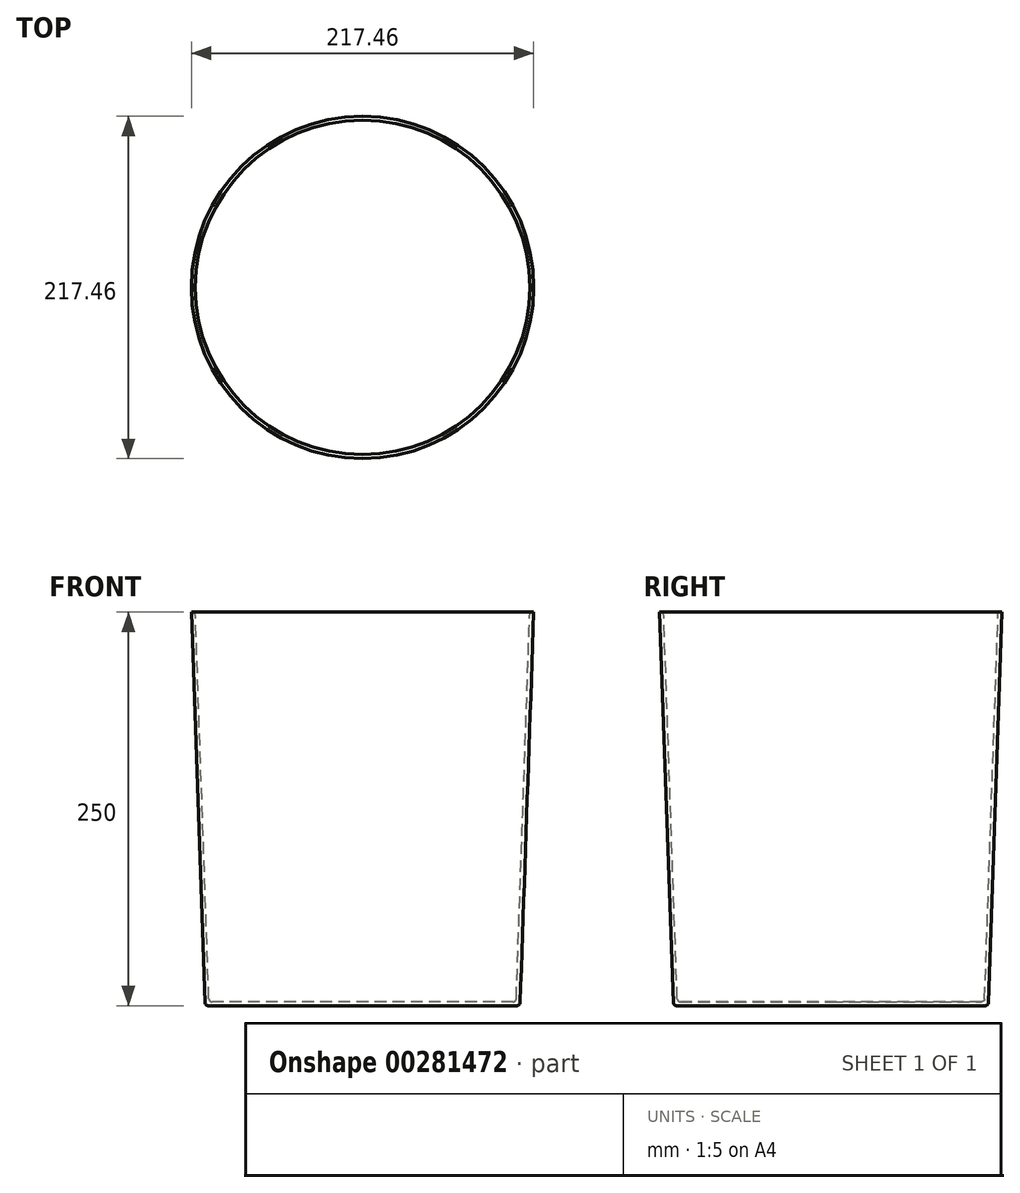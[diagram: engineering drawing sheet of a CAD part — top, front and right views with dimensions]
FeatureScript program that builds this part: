
annotation { "Feature Type Name" : "Feature", "Feature Type Description" : "" }
export const myFeature = defineFeature(function(context is Context, id is Id, definition is map)
    precondition{}
    {
        {
            var Q0;
            Q0=qCreatedBy(makeId("Top.planeOp"),FACE);
            var sketch = newSketch(context, id + "F0", { "sketchPlane" : qUnion([Q0])});
            skCircle(sketch, "E0", {"center": v(0, 0) * mm, "radius": 100 * mm});
            skSolve(sketch);
        }
        {
            var Q0;
            Q0 = qSketchRegion(id + "F0", true);
            extrude(context, id + "F1", {"entities" : qUnion([Q0]), "depth" : 250 * mm, "hasDraft" : true, "draftAngle" : 2 * degree});
        }
        {
            var Q0;
            Q0=makeQuery(id+"F1.opExtrude","CAP_FACE",FACE,{"disambiguationData":[OSD([sQuery(id+"F0.wireOp",EDGE,"E0")])],"isStart":false});
            shell(context, id + "F2", {"entities" : qUnion([Q0]), "thickness" : 2.5 * mm});
        }
        {
            var Q0;
            Q0=makeQuery(id+"F1.opExtrude","CAP_EDGE",EDGE,{"disambiguationData":[OSD([sQuery(id+"F0.wireOp",EDGE,"E0")])],"isStart":true});
            var Q1;
            {var subQ0=sQuery(id+"F0.wireOp",EDGE,"E0");Q1=makeQuery(id+"F2.opShell","OFFSET_FACE",FACE,{"disambiguationData":[OSD([subQ0]),TDD([makeQuery(id+"F1.opExtrude","CAP_FACE",FACE,{"disambiguationData":[OSD([subQ0])],"isStart":true})])]});}
            fillet(context, id + "F3", {"entities" : qUnion([Q0, Q1]), "radius" : 2 * mm, "tangentPropagation" : true, "allowEdgeOverflow" : false});
        }
    });
